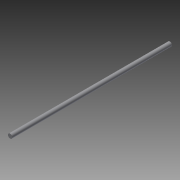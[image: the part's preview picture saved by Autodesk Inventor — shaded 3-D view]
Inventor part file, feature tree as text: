
AUTODESK INVENTOR PART (.ipt)
format: ipt  version: 2013 (Build 170138000, 138)  size: 63,488 bytes
history: native  units: in
note: dims shown in document units (in); Inventor stores cm internally (conversion verified against a paired STEP export)
features: extrude x1, sketch x1
ambient origin geometry x8: Origin, YZ Plane, XZ Plane, XY Plane, X Axis, Y Axis, Z Axis, Center Point
bodies: Solid1 (feature_tree)
feature tree (2):
  extrude  "Extrusion1"  Depth=14.0in TaperAngle=0.0deg
  sketch  "Sketch1"  dims[d0=0.375in d1=14.0in d2=0.0in]
